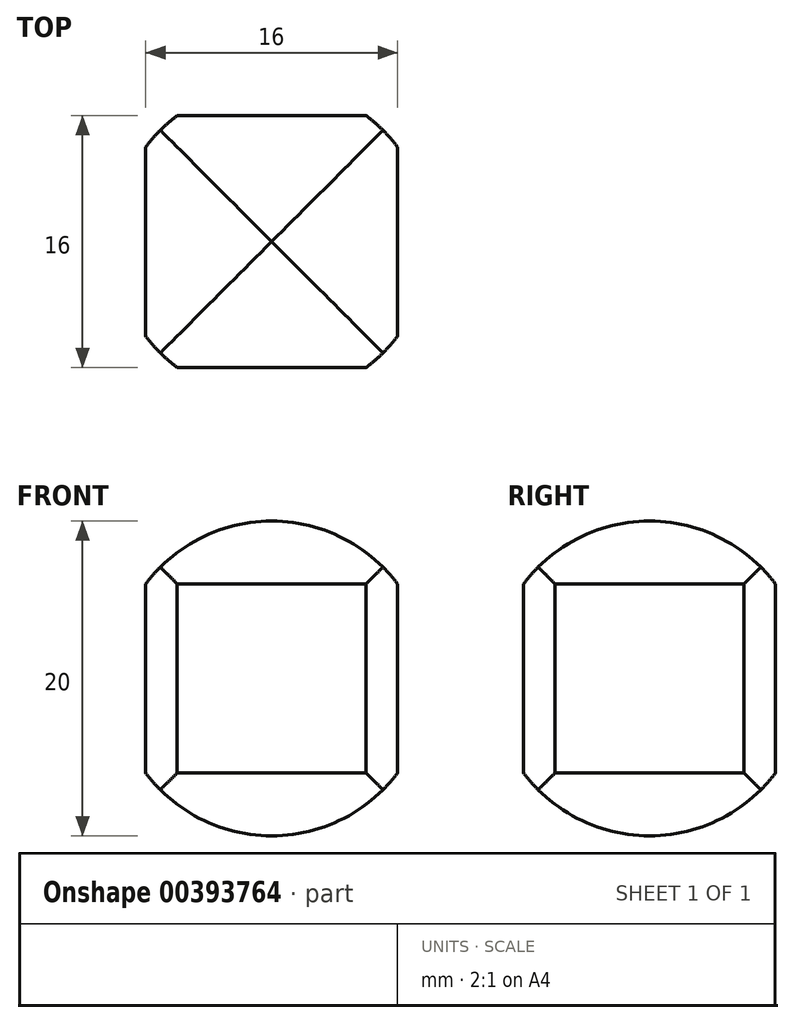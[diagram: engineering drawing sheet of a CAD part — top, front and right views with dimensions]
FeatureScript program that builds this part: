
annotation { "Feature Type Name" : "Feature", "Feature Type Description" : "" }
export const myFeature = defineFeature(function(context is Context, id is Id, definition is map)
    precondition{}
    {
        {
            var Q0;
            Q0=qCreatedBy(makeId("Front.planeOp"),FACE);
            var sketch = newSketch(context, id + "F0", { "sketchPlane" : qUnion([Q0])});
            skCircle(sketch, "E0", {"center": v(0, 0) * mm, "radius": 10 * mm});
            skLineSegment(sketch, "E1.bottom", {"start": v(10, -10) * mm, "end": v(-10, -10) * mm});
            skLineSegment(sketch, "E1.top", {"start": v(10, 10) * mm, "end": v(-10, 10) * mm});
            skLineSegment(sketch, "E1.left", {"start": v(10, -10) * mm, "end": v(10, 10) * mm});
            skLineSegment(sketch, "E1.right", {"start": v(-10, -10) * mm, "end": v(-10, 10) * mm});
            skSolve(sketch);
        }
        {
            var Q0;
            Q0=qCreatedBy(makeId("Top.planeOp"),FACE);
            var sketch = newSketch(context, id + "F1", { "sketchPlane" : qUnion([Q0])});
            skCircle(sketch, "E2", {"center": v(0, 0) * mm, "radius": 10 * mm});
            skSolve(sketch);
        }
        {
            var Q0;
            Q0=qCreatedBy(makeId("Right.planeOp"),FACE);
            var sketch = newSketch(context, id + "F2", { "sketchPlane" : qUnion([Q0])});
            skCircle(sketch, "E3", {"center": v(0, 0) * mm, "radius": 10 * mm});
            skSolve(sketch);
        }
        {
            var Q0;
            Q0=makeQuery(id+"F1.imprint","IMPRINT",FACE,{"disambiguationData":[TD([[makeQuery(id+"F1.imprint","IMPRINT",EDGE,{"derivedFrom":sQuery(id+"F1.wireOp",EDGE,"E2")}),1.0]])]});
            extrude(context, id + "F3", {"entities" : qUnion([Q0]), "endBound" : BoundingType.SYMMETRIC, "depth" : 20 * mm});
        }
        {
            var Q0;
            Q0 = qSketchRegion(id + "F2", true);
            extrude(context, id + "F4", {"entities" : qUnion([Q0]), "operationType" : NewBodyOperationType.INTERSECT, "endBound" : BoundingType.SYMMETRIC, "depth" : 20 * mm});
        }
        {
            var Q0;
            {var subQ0=sQuery(id+"F0.wireOp",EDGE,"E0");var subQ1=makeQuery(id+"F0.imprint","INTERSECT",VERTEX,{"derivedFrom":[subQ0,sQuery(id+"F0.wireOp",EDGE,"E1.top")]});Q0=makeQuery(id+"F0.imprint","IMPRINT",FACE,{"disambiguationData":[TD([[makeQuery(id+"F0.imprint","IMPRINT",EDGE,{"disambiguationData":[TD([[subQ1,1.0]])],"derivedFrom":subQ0}),1.0]])]});}
            extrude(context, id + "F5", {"entities" : qUnion([Q0]), "operationType" : NewBodyOperationType.INTERSECT, "endBound" : BoundingType.SYMMETRIC, "depth" : 20 * mm});
        }
        {
            var Q0;
            Q0=qCreatedBy(makeId("Top.planeOp"),FACE);
            var sketch = newSketch(context, id + "F6", { "sketchPlane" : qUnion([Q0])});
            skLineSegment(sketch, "E4.bottom", {"start": v(8, -8) * mm, "end": v(-8, -8) * mm});
            skLineSegment(sketch, "E4.top", {"start": v(8, 8) * mm, "end": v(-8, 8) * mm});
            skLineSegment(sketch, "E4.left", {"start": v(8, -8) * mm, "end": v(8, 8) * mm});
            skLineSegment(sketch, "E4.right", {"start": v(-8, -8) * mm, "end": v(-8, 8) * mm});
            skPoint(sketch, "E4.middle", {"position": v(0, 0) * mm});
            skSolve(sketch);
        }
        {
            var Q0;
            Q0 = qSketchRegion(id + "F6", true);
            extrude(context, id + "F7", {"entities" : qUnion([Q0]), "operationType" : NewBodyOperationType.INTERSECT, "endBound" : BoundingType.SYMMETRIC, "depth" : 20 * mm});
        }
    });
